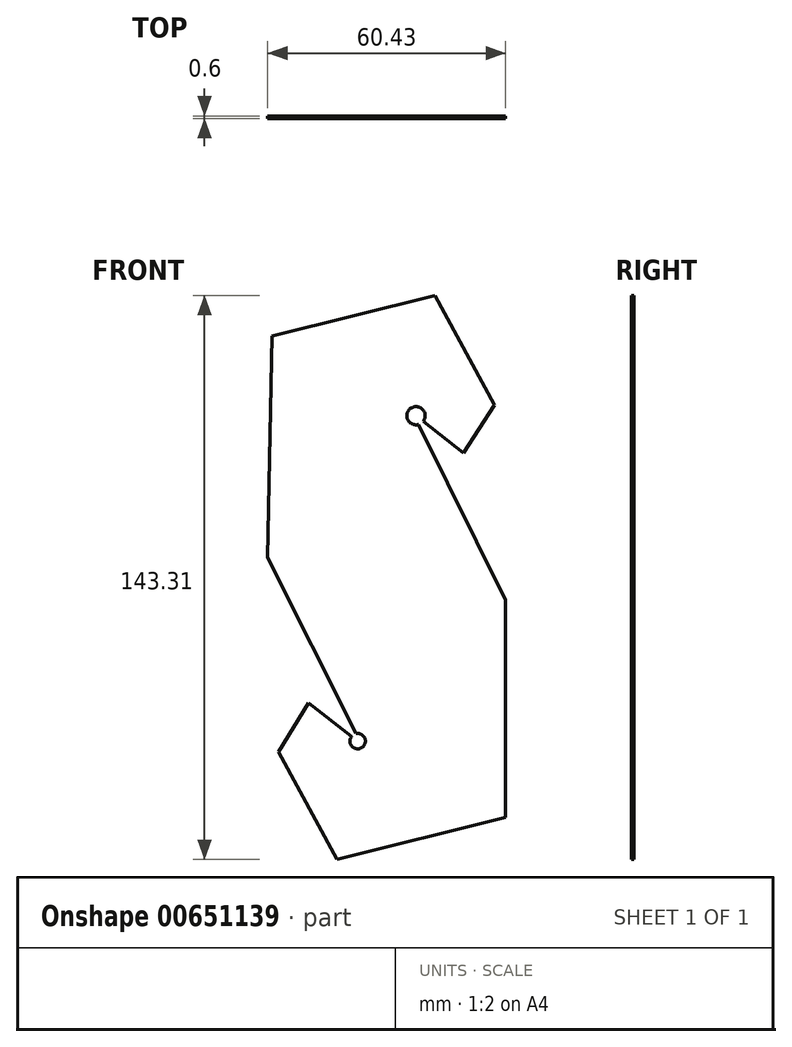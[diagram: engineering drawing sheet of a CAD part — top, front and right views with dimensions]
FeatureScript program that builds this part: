
annotation { "Feature Type Name" : "Feature", "Feature Type Description" : "" }
export const myFeature = defineFeature(function(context is Context, id is Id, definition is map)
    precondition{}
    {
        {
            var Q0;
            Q0=qCreatedBy(makeId("Front.planeOp"),FACE);
            var sketch = newSketch(context, id + "F0", { "sketchPlane" : qUnion([Q0])});
            skLineSegment(sketch, "E0", {"start": v(-66.8, 61.11) * mm, "end": v(-25.49, 71.36) * mm});
            skLineSegment(sketch, "E1", {"start": v(-25.49, 71.36) * mm, "end": v(-10.31, 43.52) * mm});
            skLineSegment(sketch, "E2", {"start": v(-10.31, 43.52) * mm, "end": v(-18.22, 31.34) * mm});
            skLineSegment(sketch, "E3", {"start": v(-18.22, 31.34) * mm, "end": v(-28.38, 39.39) * mm});
            skLineSegment(sketch, "E4", {"start": v(-29.6, 38.56) * mm, "end": v(-7.5, -6) * mm});
            skLineSegment(sketch, "E5", {"start": v(-7.5, -6) * mm, "end": v(-7.5, -61.24) * mm});
            skLineSegment(sketch, "E6", {"start": v(-7.5, -61.24) * mm, "end": v(-50.26, -71.95) * mm});
            skLineSegment(sketch, "E7", {"start": v(-50.26, -71.95) * mm, "end": v(-65.19, -44.6) * mm});
            skLineSegment(sketch, "E8", {"start": v(-65.19, -44.6) * mm, "end": v(-57.52, -32.17) * mm});
            skLineSegment(sketch, "E9", {"start": v(-57.52, -32.17) * mm, "end": v(-46.58, -40.62) * mm});
            skLineSegment(sketch, "E10", {"start": v(-45.55, -39.97) * mm, "end": v(-67.94, 4.81) * mm});
            skLineSegment(sketch, "E11", {"start": v(-67.9, 6.63) * mm, "end": v(-66.8, 61.11) * mm});
            skLineSegment(sketch, "E12", {"start": v(-67.94, 4.81) * mm, "end": v(-7.5, -6) * mm});
            skLineSegment(sketch, "E13", {"start": v(-66.54, 2) * mm, "end": v(-7.5, -8.16) * mm});
            skPoint(sketch, "E14", {"position": v(-67.85, 7.37) * mm});
            skPoint(sketch, "E15", {"position": v(-67.9, 6.63) * mm});
            skPoint(sketch, "E16", {"position": v(-63.91, 6.73) * mm});
            skLineSegment(sketch, "E17", {"start": v(-67.94, 4.81) * mm, "end": v(-67.9, 6.63) * mm});
            skLineSegment(sketch, "E18", {"start": v(-9.03, -2.93) * mm, "end": v(-67.9, 6.63) * mm});
            skLineSegment(sketch, "E19", {"start": v(-67.2, 3.32) * mm, "end": v(-7.5, -6.95) * mm});
            skLineSegment(sketch, "E20", {"start": v(-67.85, 7.37) * mm, "end": v(-9.37, -2.23) * mm});
            skLineSegment(sketch, "E21", {"start": v(-65.95, 0.84) * mm, "end": v(-7.5, -9.58) * mm});
            skPoint(sketch, "E22.end.orphan", {"position": v(-67.85, 5.9) * mm});
            skLineSegment(sketch, "E23", {"start": v(-67.92, 5.72) * mm, "end": v(-8.35, -4.3) * mm});
            skArc(sketch, "E24", {"start": v(-28.38, 39.39) * mm, "mid": v(-31.54, 42.71) * mm, "end": v(-29.6, 38.56) * mm});
            skArc(sketch, "E25", {"start": v(-46.58, -40.62) * mm, "mid": v(-44.02, -43.52) * mm, "end": v(-45.55, -39.97) * mm});
            skSolve(sketch);
        }
        {
            var Q0;
            Q0 = qSketchRegion(id + "F0", true);
            extrude(context, id + "F1", {"entities" : qUnion([Q0]), "depth" : 0.6 * mm, "offsetDistance" : 25 * mm});
        }
    });
